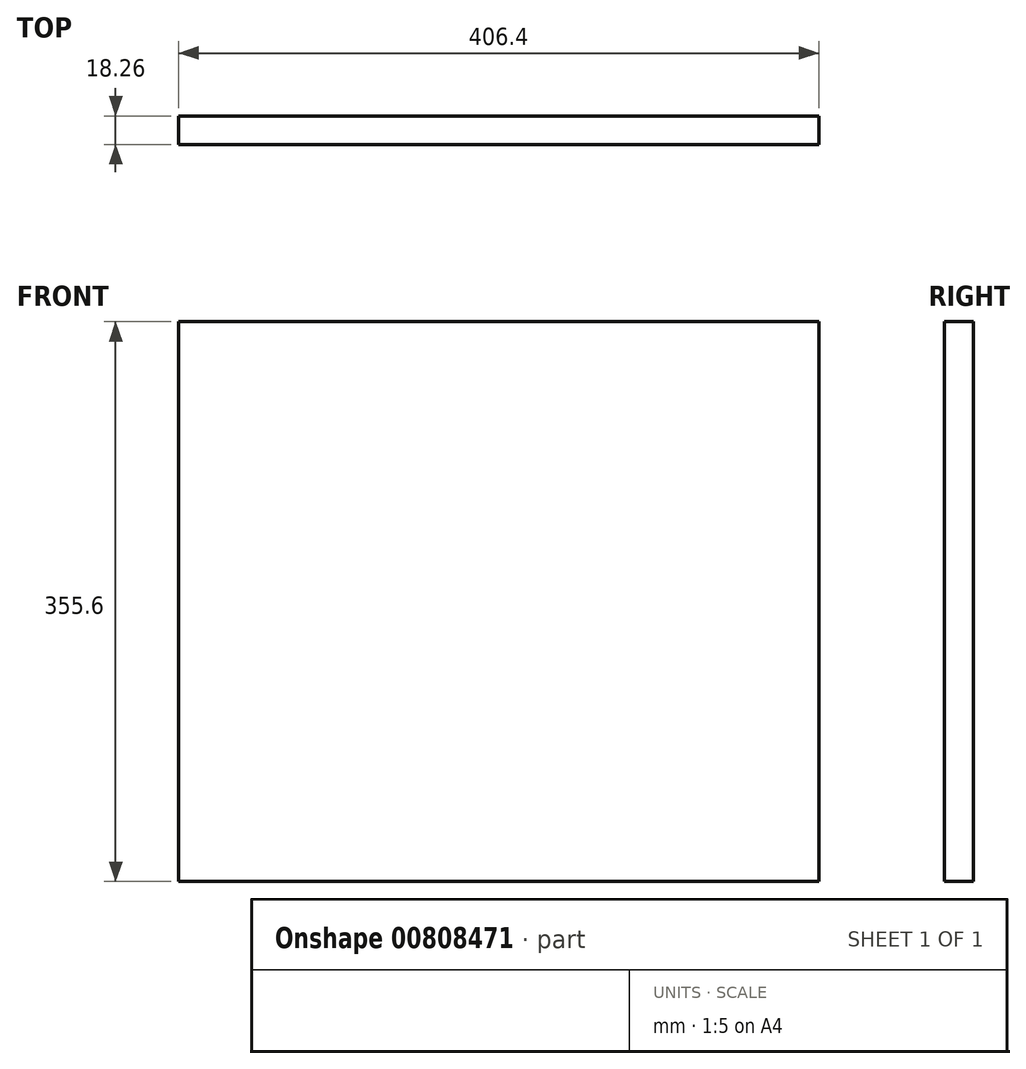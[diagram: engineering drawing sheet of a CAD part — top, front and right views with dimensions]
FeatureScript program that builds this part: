
annotation { "Feature Type Name" : "Feature", "Feature Type Description" : "" }
export const myFeature = defineFeature(function(context is Context, id is Id, definition is map)
    precondition{}
    {
        {
            var Q0;
            Q0=qCreatedBy(makeId("Front.planeOp"),FACE);
            var sketch = newSketch(context, id + "F0", { "sketchPlane" : qUnion([Q0])});
            skLineSegment(sketch, "E0.bottom", {"start": v(203.2, 177.8) * mm, "end": v(-203.2, 177.8) * mm});
            skLineSegment(sketch, "E0.top", {"start": v(203.2, -177.8) * mm, "end": v(-203.2, -177.8) * mm});
            skLineSegment(sketch, "E0.left", {"start": v(203.2, 177.8) * mm, "end": v(203.2, -177.8) * mm});
            skLineSegment(sketch, "E0.right", {"start": v(-203.2, 177.8) * mm, "end": v(-203.2, -177.8) * mm});
            skPoint(sketch, "E0.middle", {"position": v(0, 0) * mm});
            skSolve(sketch);
        }
        {
            var Q0;
            Q0 = qSketchRegion(id + "F0", true);
            extrude(context, id + "F1", {"entities" : qUnion([Q0]), "depth" : 18.26 * mm, "offsetDistance" : 25.4 * mm});
        }
    });
